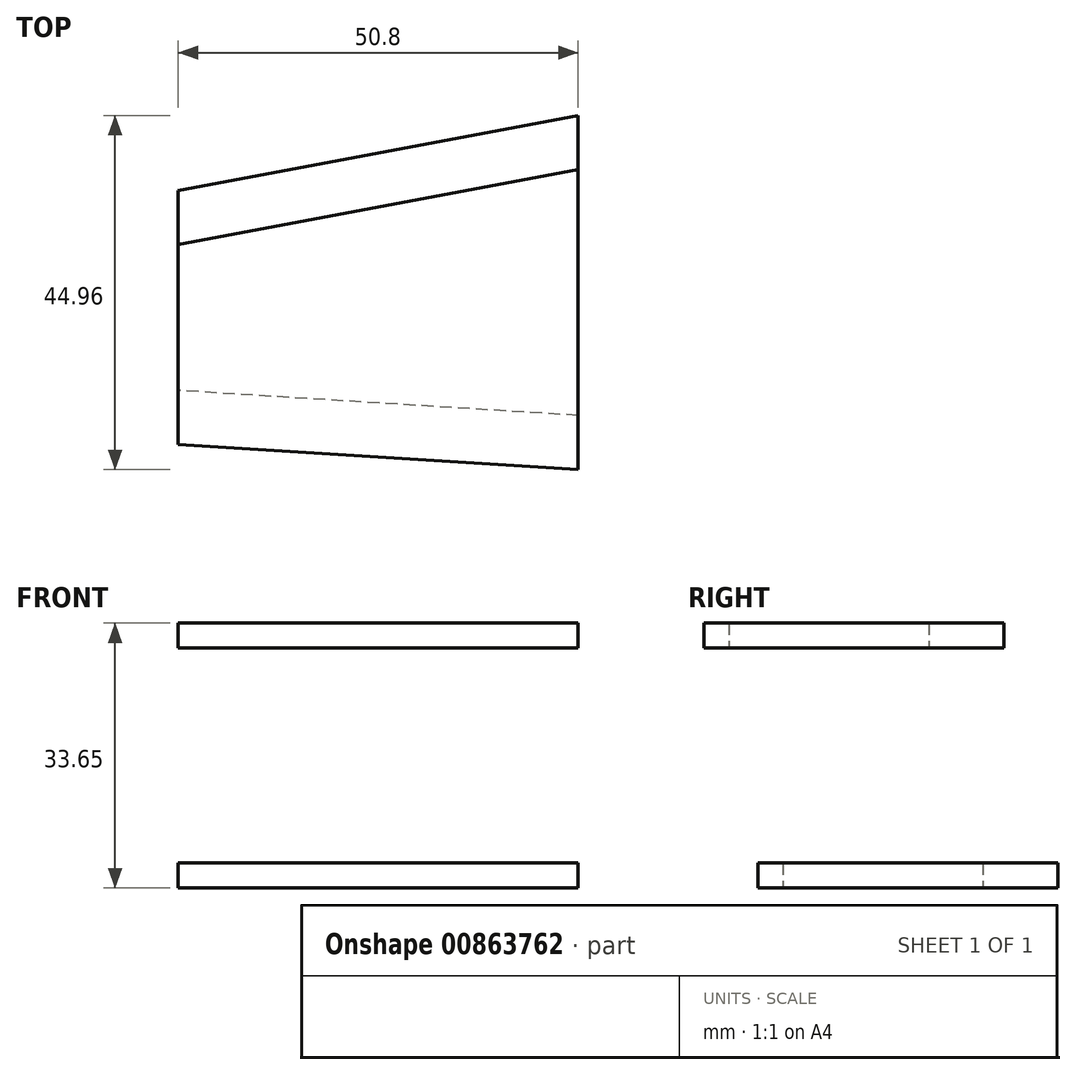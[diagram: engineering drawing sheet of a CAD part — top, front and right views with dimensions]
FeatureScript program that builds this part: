
annotation { "Feature Type Name" : "Feature", "Feature Type Description" : "" }
export const myFeature = defineFeature(function(context is Context, id is Id, definition is map)
    precondition{}
    {
        {
            var Q0;
            Q0=qCreatedBy(makeId("Top.planeOp"),FACE);
            var sketch = newSketch(context, id + "F0", { "sketchPlane" : qUnion([Q0])});
            skLineSegment(sketch, "E0.left", {"start": v(-68.4, -11.48) * mm, "end": v(-68.4, -36.88) * mm});
            skLineSegment(sketch, "E0.right", {"start": v(33.2, -11.48) * mm, "end": v(33.2, -36.88) * mm});
            skPoint(sketch, "E0.bottom.start.orphan", {"position": v(-68.4, 36.14) * mm});
            skPoint(sketch, "E1.orphan", {"position": v(33.2, 36.14) * mm});
            skPoint(sketch, "E2", {"position": v(-68.4, -36.88) * mm});
            skPoint(sketch, "E3", {"position": v(33.2, -36.88) * mm});
            skPoint(sketch, "E4", {"position": v(-68.4, -11.48) * mm});
            skPoint(sketch, "E5", {"position": v(33.2, -11.48) * mm});
            skPoint(sketch, "E6", {"position": v(-17.6, -1.96) * mm});
            skLineSegment(sketch, "E7", {"start": v(-68.4, -11.48) * mm, "end": v(-17.6, -1.96) * mm});
            skLineSegment(sketch, "E8", {"start": v(33.2, -11.48) * mm, "end": v(-17.6, -1.96) * mm});
            skPoint(sketch, "E9.orphan", {"position": v(-68.4, -1.96) * mm});
            skPoint(sketch, "E10.orphan", {"position": v(33.2, -1.96) * mm});
            skPoint(sketch, "E11", {"position": v(-17.6, -40.06) * mm});
            skLineSegment(sketch, "E12", {"start": v(-17.6, -40.06) * mm, "end": v(-68.4, -36.88) * mm});
            skLineSegment(sketch, "E13", {"start": v(-17.6, -40.06) * mm, "end": v(33.2, -36.88) * mm});
            skPoint(sketch, "E14.orphan", {"position": v(-68.4, -40.06) * mm});
            skPoint(sketch, "E15.orphan", {"position": v(33.2, -40.06) * mm});
            skLineSegment(sketch, "E16", {"start": v(-17.6, -1.96) * mm, "end": v(-17.6, -40.06) * mm});
            skSolve(sketch);
        }
        {
            var Q0;
            Q0=makeQuery(id+"F0.imprint","IMPRINT",FACE,{"disambiguationData":[TD([[makeQuery(id+"F0.imprint","IMPRINT",EDGE,{"derivedFrom":sQuery(id+"F0.wireOp",EDGE,"E0.left")}),1.0]])]});
            extrude(context, id + "F1", {"entities" : qUnion([Q0]), "depth" : 3.17 * mm, "offsetDistance" : 25.4 * mm});
        }
        {
            var Q0;
            Q0=makeQuery(id+"F1.opExtrude","SWEPT_BODY",BODY,{"disambiguationData":[OSD([sQuery(id+"F0.wireOp",EDGE,"E0.left"),sQuery(id+"F0.wireOp",EDGE,"E7"),sQuery(id+"F0.wireOp",EDGE,"E12"),sQuery(id+"F0.wireOp",EDGE,"E16")])]});
            transform(context, id + "F2", {"entities" : qUnion([Q0]), "transformType" : TransformType.TRANSLATION_3D, "dx" : 0 * mm, "dy" : 6.86 * mm, "dz" : -30.48 * mm, "makeCopy" : true});
        }
    });
